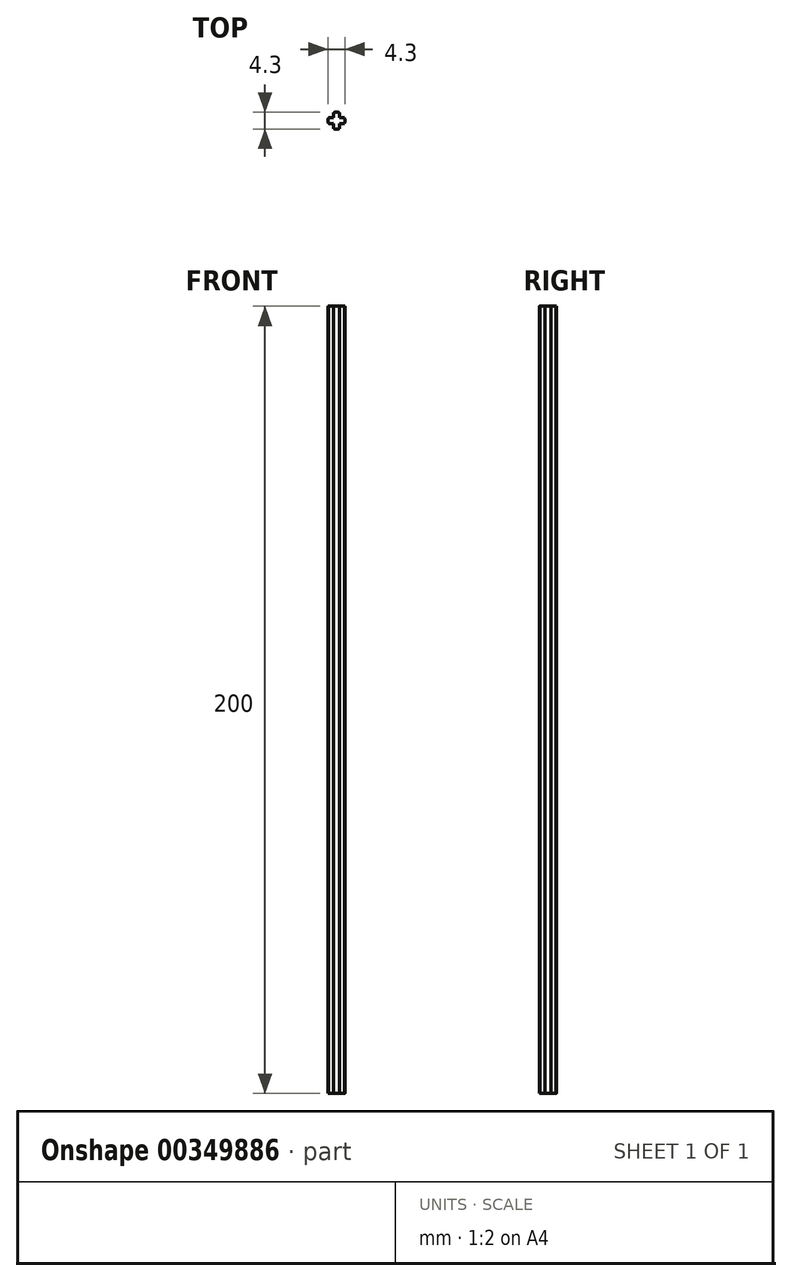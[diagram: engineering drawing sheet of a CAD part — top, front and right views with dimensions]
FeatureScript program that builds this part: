
annotation { "Feature Type Name" : "Feature", "Feature Type Description" : "" }
export const myFeature = defineFeature(function(context is Context, id is Id, definition is map)
    precondition{}
    {
        {
            var Q0;
            Q0=qCreatedBy(makeId("Top.planeOp"),FACE);
            var sketch = newSketch(context, id + "F0", { "sketchPlane" : qUnion([Q0])});
            skCircle(sketch, "E0", {"center": v(0, 0) * mm, "radius": 2.15 * mm});
            skLineSegment(sketch, "E1", {"start": v(-0.72, 2.02) * mm, "end": v(-0.72, 0.72) * mm});
            skLineSegment(sketch, "E2", {"start": v(-0.72, 0.72) * mm, "end": v(-2.02, 0.72) * mm});
            skLineSegment(sketch, "E3", {"start": v(-2.02, -0.72) * mm, "end": v(-0.72, -0.72) * mm});
            skLineSegment(sketch, "E4", {"start": v(-0.72, -0.72) * mm, "end": v(-0.72, -2.02) * mm});
            skLineSegment(sketch, "E5", {"start": v(0.72, -2.02) * mm, "end": v(0.72, -0.72) * mm});
            skLineSegment(sketch, "E6", {"start": v(0.72, -0.72) * mm, "end": v(2.02, -0.72) * mm});
            skLineSegment(sketch, "E7", {"start": v(0.72, 2.02) * mm, "end": v(0.72, 0.72) * mm});
            skLineSegment(sketch, "E8", {"start": v(0.72, 0.72) * mm, "end": v(2.02, 0.72) * mm});
            skSolve(sketch);
        }
        {
            var Q0;
            {var subQ4=sQuery(id+"F0.wireOp",EDGE,"E1");Q0=makeQuery(id+"F0.imprint","IMPRINT",FACE,{"disambiguationData":[TD([[makeQuery(id+"F0.imprint","IMPRINT",EDGE,{"derivedFrom":subQ4}),1.0]])]});}
            extrude(context, id + "F1", {"entities" : qUnion([Q0]), "depth" : 200 * mm});
        }
    });
